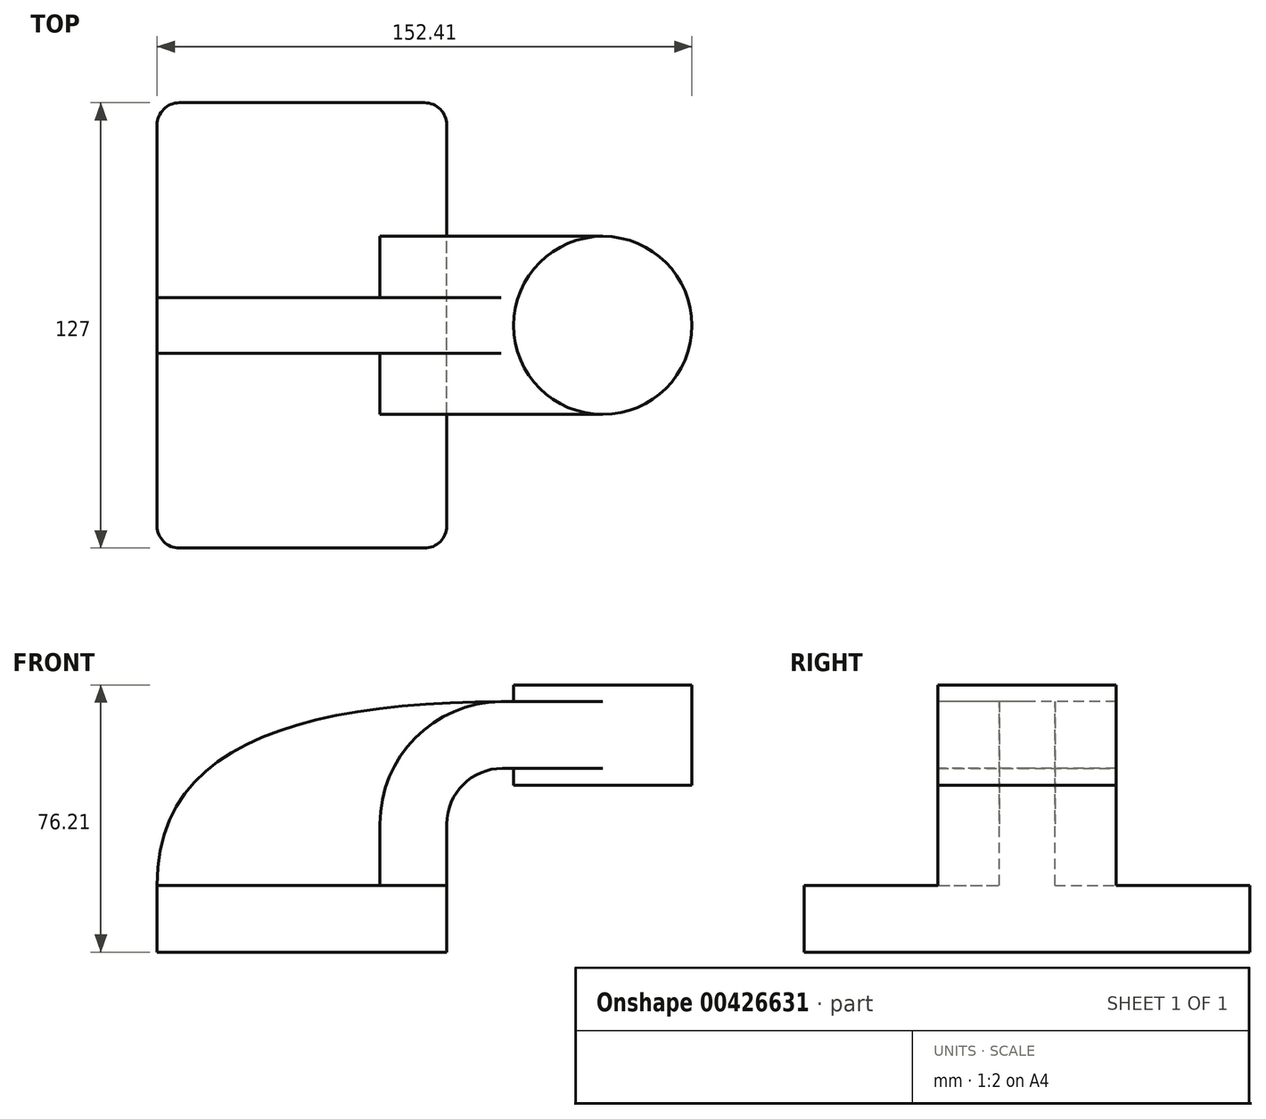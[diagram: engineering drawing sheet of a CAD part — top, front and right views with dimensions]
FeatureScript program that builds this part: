
annotation { "Feature Type Name" : "Feature", "Feature Type Description" : "" }
export const myFeature = defineFeature(function(context is Context, id is Id, definition is map)
    precondition{}
    {
        {
            var Q0;
            Q0=qCreatedBy(makeId("Front.planeOp"),FACE);
            var sketch = newSketch(context, id + "F0", { "sketchPlane" : qUnion([Q0])});
            skLineSegment(sketch, "E0.bottom", {"start": v(41.28, -9.52) * mm, "end": v(-41.27, -9.52) * mm});
            skLineSegment(sketch, "E0.top", {"start": v(41.27, 9.53) * mm, "end": v(-41.28, 9.53) * mm});
            skLineSegment(sketch, "E0.left", {"start": v(41.28, -9.52) * mm, "end": v(41.28, 9.53) * mm});
            skLineSegment(sketch, "E0.right", {"start": v(-41.27, -9.52) * mm, "end": v(-41.28, 9.53) * mm});
            skPoint(sketch, "E0.middle", {"position": v(0, 0) * mm});
            skLineSegment(sketch, "E1.bottom", {"start": v(111.13, 38.1) * mm, "end": v(60.33, 38.1) * mm});
            skLineSegment(sketch, "E1.top", {"start": v(111.13, 66.68) * mm, "end": v(60.33, 66.68) * mm});
            skLineSegment(sketch, "E1.left", {"start": v(111.13, 38.1) * mm, "end": v(111.13, 66.68) * mm});
            skLineSegment(sketch, "E1.right", {"start": v(60.33, 38.1) * mm, "end": v(60.33, 66.68) * mm});
            skPoint(sketch, "E1.middle", {"position": v(85.72, 52.39) * mm});
            skLineSegment(sketch, "E2", {"start": v(41.27, 9.53) * mm, "end": v(41.27, 27) * mm});
            skArc(sketch, "E3", {"start": v(41.27, 27) * mm, "mid": v(45.92, 38.23) * mm, "end": v(57.15, 42.88) * mm});
            skLineSegment(sketch, "E4", {"start": v(57.15, 42.88) * mm, "end": v(85.73, 42.88) * mm});
            skLineSegment(sketch, "E5.0", {"start": v(57.15, 61.93) * mm, "end": v(85.95, 61.93) * mm});
            skArc(sketch, "E5.1", {"start": v(22.23, 27) * mm, "mid": v(32.45, 51.7) * mm, "end": v(57.15, 61.93) * mm});
            skLineSegment(sketch, "E5.2", {"start": v(22.22, 9.53) * mm, "end": v(22.22, 27) * mm});
            skLineSegment(sketch, "E6", {"start": v(85.73, 42.88) * mm, "end": v(85.73, 66.68) * mm});
            skFitSpline(sketch, "E7", {"points": [v(-41.28, 9.53) * mm, v(57.15, 61.93) * mm], "startDerivative": vector(-0.58, 121.52) * mm, "endDerivative": vector(171.45, 1.06) * mm});
            skLineSegment(sketch, "E8", {"start": v(85.72, 38.1) * mm, "end": v(85.73, 42.88) * mm});
            skSolve(sketch);
        }
        {
            var Q0;
            Q0=makeQuery(id+"F0.imprint","IMPRINT",FACE,{"disambiguationData":[TD([[makeQuery(id+"F0.imprint","IMPRINT",EDGE,{"derivedFrom":sQuery(id+"F0.wireOp",EDGE,"E0.bottom")}),-1.0]])]});
            extrude(context, id + "F1", {"entities" : qUnion([Q0]), "endBound" : BoundingType.SYMMETRIC, "depth" : 127 * mm});
        }
        {
            var Q0;
            {var subQ6=sQuery(id+"F0.wireOp",EDGE,"E2");Q0=makeQuery(id+"F0.imprint","IMPRINT",FACE,{"disambiguationData":[TD([[makeQuery(id+"F0.imprint","IMPRINT",EDGE,{"derivedFrom":subQ6}),1.0]])]});}
            var Q1;
            {var subQ0=sQuery(id+"F0.wireOp",EDGE,"E4");var subQ1=sQuery(id+"F0.wireOp",EDGE,"E1.right");var subQ2=makeQuery(id+"F0.imprint","INTERSECT",VERTEX,{"derivedFrom":[subQ1,subQ0]});Q1=makeQuery(id+"F0.imprint","IMPRINT",FACE,{"disambiguationData":[TD([[makeQuery(id+"F0.imprint","IMPRINT",EDGE,{"disambiguationData":[TD([[subQ2,-1.0]])],"derivedFrom":subQ1}),-1.0]])]});}
            extrude(context, id + "F2", {"entities" : qUnion([Q0, Q1]), "operationType" : NewBodyOperationType.ADD, "endBound" : BoundingType.SYMMETRIC, "depth" : 50.8 * mm});
        }
        {
            var Q0;
            {var subQ3=sQuery(id+"F0.wireOp",EDGE,"E5.2");Q0=makeQuery(id+"F0.imprint","IMPRINT",FACE,{"disambiguationData":[TD([[makeQuery(id+"F0.imprint","IMPRINT",EDGE,{"derivedFrom":subQ3}),1.0]])]});}
            extrude(context, id + "F3", {"entities" : qUnion([Q0]), "operationType" : NewBodyOperationType.ADD, "endBound" : BoundingType.SYMMETRIC, "depth" : 15.88 * mm});
        }
        {
            var Q0;
            {var subQ0=sQuery(id+"F0.wireOp",EDGE,"E1.left");Q0=makeQuery(id+"F0.imprint","IMPRINT",FACE,{"disambiguationData":[TD([[makeQuery(id+"F0.imprint","IMPRINT",EDGE,{"derivedFrom":subQ0}),1.0]])]});}
            var Q1;
            Q1=sQuery(id+"F0.wireOp",EDGE,"E6");
            revolve(context, id + "F4", {"operationType" : NewBodyOperationType.ADD, "entities" : qUnion([Q0]), "axis" : qUnion([Q1]), "revolveType" : RevolveType.FULL});
        }
        {
            var Q0;
            Q0=makeQuery(id+"F1.opExtrude","CAP_EDGE",EDGE,{"disambiguationData":[OSD([sQuery(id+"F0.wireOp",EDGE,"E0.left")])],"isStart":false});
            var Q1;
            Q1=makeQuery(id+"F1.opExtrude","CAP_EDGE",EDGE,{"disambiguationData":[OSD([sQuery(id+"F0.wireOp",EDGE,"E0.right")])],"isStart":false});
            var Q2;
            Q2=makeQuery(id+"F1.opExtrude","CAP_EDGE",EDGE,{"disambiguationData":[OSD([sQuery(id+"F0.wireOp",EDGE,"E0.right")])],"isStart":true});
            var Q3;
            Q3=makeQuery(id+"F1.opExtrude","CAP_EDGE",EDGE,{"disambiguationData":[OSD([sQuery(id+"F0.wireOp",EDGE,"E0.left")])],"isStart":true});
            fillet(context, id + "F5", {"entities" : qUnion([Q0, Q1, Q2, Q3]), "radius" : 6.35 * mm, "tangentPropagation" : true, "allowEdgeOverflow" : false});
        }
    });
